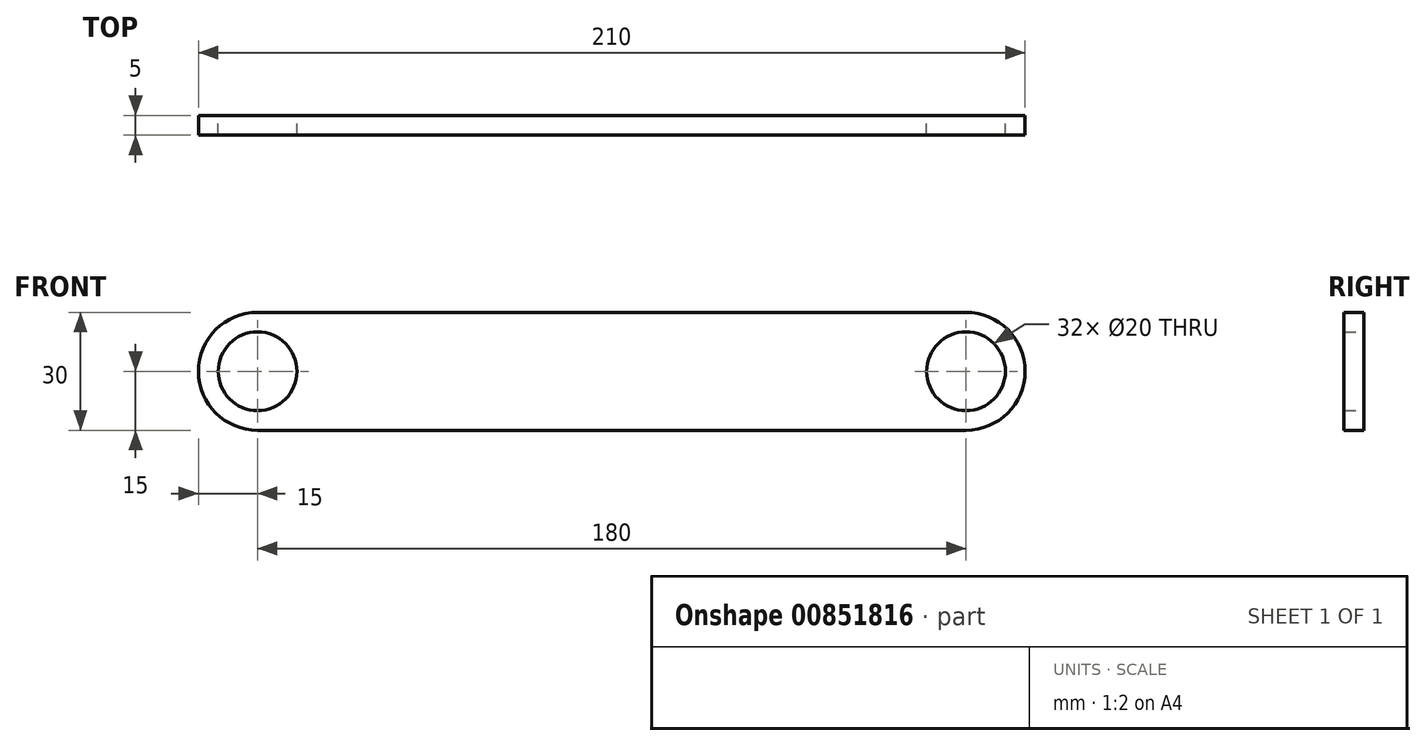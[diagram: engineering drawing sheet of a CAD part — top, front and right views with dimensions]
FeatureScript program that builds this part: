
annotation { "Feature Type Name" : "Feature", "Feature Type Description" : "" }
export const myFeature = defineFeature(function(context is Context, id is Id, definition is map)
    precondition{}
    {
        {
            var Q0;
            Q0=qCreatedBy(makeId("Front.planeOp"),FACE);
            var sketch = newSketch(context, id + "F0", { "sketchPlane" : qUnion([Q0])});
            skLineSegment(sketch, "E0", {"start": v(0, 0) * mm, "end": v(180, 0) * mm, "construction": true});
            skCircle(sketch, "E1", {"center": v(0, 0) * mm, "radius": 15 * mm});
            skCircle(sketch, "E2", {"center": v(180, 0) * mm, "radius": 15 * mm});
            skLineSegment(sketch, "E3", {"start": v(0, 15) * mm, "end": v(180, 15) * mm});
            skLineSegment(sketch, "E4", {"start": v(0, -15) * mm, "end": v(180, -15) * mm});
            skCircle(sketch, "E5", {"center": v(0, 0) * mm, "radius": 10 * mm});
            skCircle(sketch, "E6", {"center": v(180, 0) * mm, "radius": 10 * mm});
            skSolve(sketch);
        }
        {
            var Q0;
            {var subQ0=sQuery(id+"F0.wireOp",EDGE,"E3");Q0=makeQuery(id+"F0.imprint","IMPRINT",FACE,{"disambiguationData":[TD([[makeQuery(id+"F0.imprint","IMPRINT",EDGE,{"derivedFrom":subQ0}),-1.0]])]});}
            var Q1;
            Q1=makeQuery(id+"F0.imprint","IMPRINT",FACE,{"disambiguationData":[TD([[makeQuery(id+"F0.imprint","IMPRINT",EDGE,{"derivedFrom":sQuery(id+"F0.wireOp",EDGE,"E5")}),-1.0]])]});
            var Q2;
            Q2=makeQuery(id+"F0.imprint","IMPRINT",FACE,{"disambiguationData":[TD([[makeQuery(id+"F0.imprint","IMPRINT",EDGE,{"derivedFrom":sQuery(id+"F0.wireOp",EDGE,"E6")}),-1.0]])]});
            extrude(context, id + "F1", {"entities" : qUnion([Q0, Q1, Q2]), "endBound" : BoundingType.SYMMETRIC, "depth" : 5 * mm, "offsetDistance" : 25 * mm});
        }
    });
